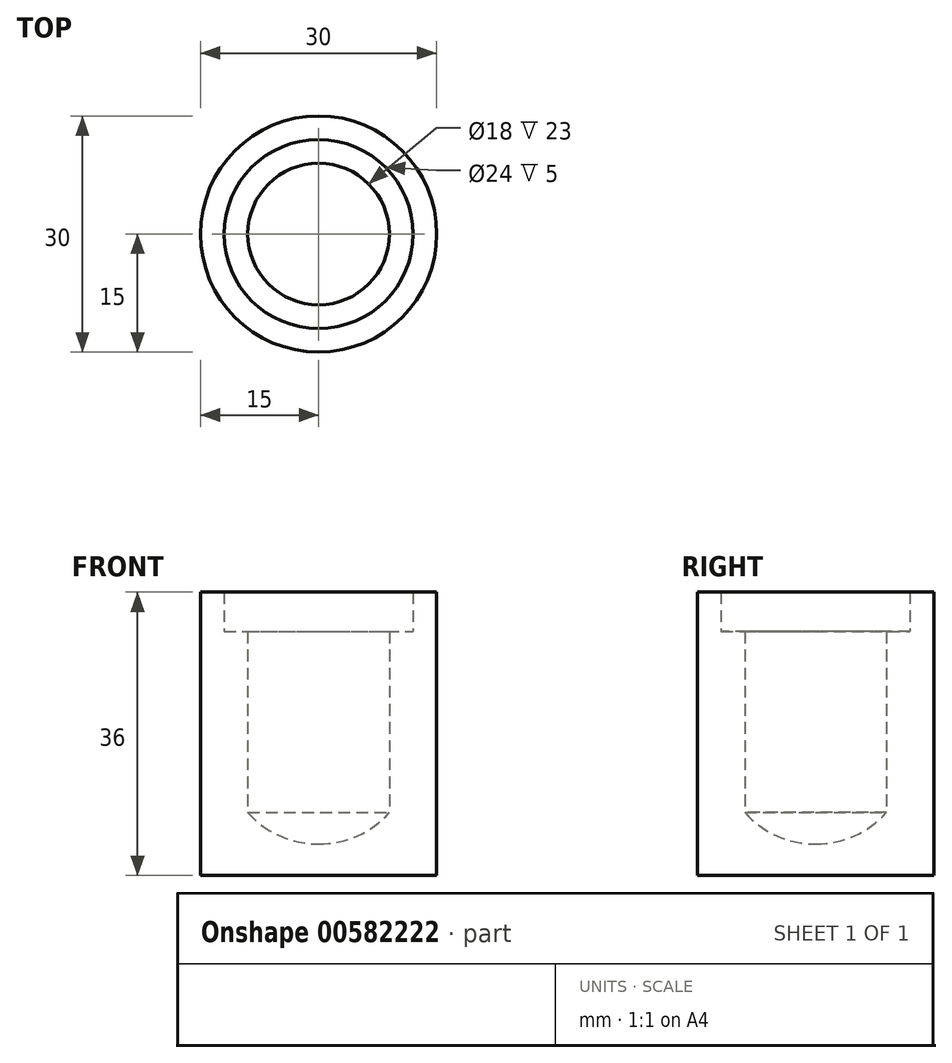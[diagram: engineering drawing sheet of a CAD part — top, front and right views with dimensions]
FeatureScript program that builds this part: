
annotation { "Feature Type Name" : "Feature", "Feature Type Description" : "" }
export const myFeature = defineFeature(function(context is Context, id is Id, definition is map)
    precondition{}
    {
        {
            var Q0;
            Q0=qCreatedBy(makeId("Front.planeOp"),FACE);
            var sketch = newSketch(context, id + "F0", { "sketchPlane" : qUnion([Q0]), "disableImprinting" : false});
            skLineSegment(sketch, "E0.top", {"start": v(15, -4) * mm, "end": v(-15, -4) * mm});
            skLineSegment(sketch, "E0.left", {"start": v(15, 4) * mm, "end": v(15, -4) * mm});
            skLineSegment(sketch, "E0.right", {"start": v(-15, 4) * mm, "end": v(-15, -4) * mm});
            skPoint(sketch, "E0.middle", {"position": v(0, 0) * mm});
            skLineSegment(sketch, "E1.left", {"start": v(-15, 4) * mm, "end": v(-15, 29) * mm});
            skLineSegment(sketch, "E1.right", {"start": v(-9, 4) * mm, "end": v(-9, 27) * mm});
            skLineSegment(sketch, "E2.left", {"start": v(15, 4) * mm, "end": v(15, 27) * mm});
            skLineSegment(sketch, "E2.right", {"start": v(9, 4) * mm, "end": v(9, 27) * mm});
            skPoint(sketch, "E3.oppositeSnap0", {"position": v(12, 27) * mm});
            skLineSegment(sketch, "E3.top", {"start": v(15, 32) * mm, "end": v(12, 32) * mm});
            skLineSegment(sketch, "E3.left", {"start": v(15, 27) * mm, "end": v(15, 32) * mm});
            skLineSegment(sketch, "E3.right", {"start": v(12, 27) * mm, "end": v(12, 32) * mm});
            skLineSegment(sketch, "E4.top", {"start": v(-15, 32) * mm, "end": v(-12, 32) * mm});
            skLineSegment(sketch, "E4.left", {"start": v(-15, 29) * mm, "end": v(-15, 32) * mm});
            skLineSegment(sketch, "E4.right", {"start": v(-12, 27) * mm, "end": v(-12, 32) * mm});
            skArc(sketch, "E5", {"start": v(-9, 4) * mm, "mid": v(0, 0) * mm, "end": v(9, 4) * mm});
            skLineSegment(sketch, "E6", {"start": v(12, 27) * mm, "end": v(9, 27) * mm});
            skLineSegment(sketch, "E7", {"start": v(-12, 27) * mm, "end": v(-9, 27) * mm});
            skLineSegment(sketch, "E8", {"start": v(0, -4) * mm, "end": v(0, 0) * mm});
            skSolve(sketch);
        }
        {
            var Q0;
            {var subQ1=sQuery(id+"F0.wireOp",EDGE,"E0.right");Q0=makeQuery(id+"F0.imprint","IMPRINT",FACE,{"disambiguationData":[TD([[makeQuery(id+"F0.imprint","IMPRINT",EDGE,{"derivedFrom":subQ1}),1.0]])]});}
            var Q1;
            Q1=sQuery(id+"F0.wireOp",EDGE,"E8");
            revolve(context, id + "F1", {"entities" : qUnion([Q0]), "axis" : qUnion([Q1]), "revolveType" : RevolveType.FULL});
        }
    });
